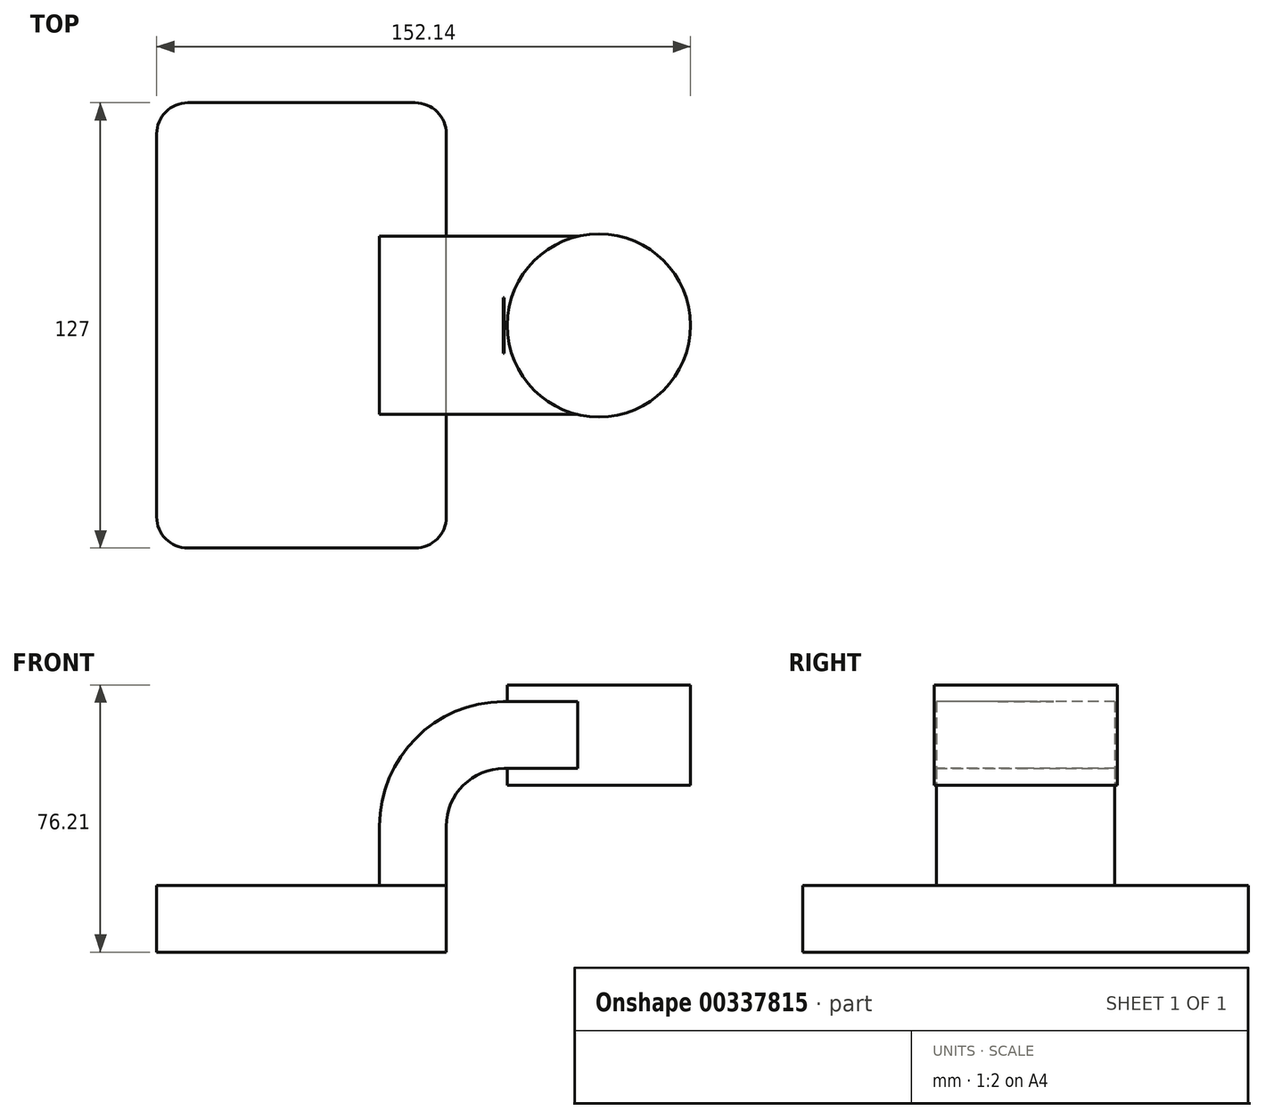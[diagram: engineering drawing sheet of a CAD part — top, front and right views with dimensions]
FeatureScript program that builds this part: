
annotation { "Feature Type Name" : "Feature", "Feature Type Description" : "" }
export const myFeature = defineFeature(function(context is Context, id is Id, definition is map)
    precondition{}
    {
        {
            var Q0;
            Q0=qCreatedBy(makeId("Front.planeOp"),FACE);
            var sketch = newSketch(context, id + "F0", { "sketchPlane" : qUnion([Q0])});
            skLineSegment(sketch, "E0.bottom", {"start": v(41.28, -9.52) * mm, "end": v(-41.28, -9.53) * mm});
            skLineSegment(sketch, "E0.top", {"start": v(41.28, 9.53) * mm, "end": v(-41.28, 9.53) * mm});
            skLineSegment(sketch, "E0.left", {"start": v(41.28, -9.52) * mm, "end": v(41.28, 9.53) * mm});
            skLineSegment(sketch, "E0.right", {"start": v(-41.28, -9.53) * mm, "end": v(-41.28, 9.53) * mm});
            skPoint(sketch, "E0.middle", {"position": v(0, 0) * mm});
            skLineSegment(sketch, "E1.bottom", {"start": v(110.87, 66.68) * mm, "end": v(60.07, 66.68) * mm});
            skLineSegment(sketch, "E1.top", {"start": v(110.87, 38.1) * mm, "end": v(60.07, 38.1) * mm});
            skLineSegment(sketch, "E1.left", {"start": v(60.07, 38.1) * mm, "end": v(60.07, 66.68) * mm});
            skLineSegment(sketch, "E1.right", {"start": v(110.87, 38.1) * mm, "end": v(110.87, 66.68) * mm});
            skPoint(sketch, "E1.middle", {"position": v(85.47, 52.39) * mm});
            skLineSegment(sketch, "E2", {"start": v(41.28, 9.53) * mm, "end": v(41.28, 26.37) * mm});
            skArc(sketch, "E3", {"start": v(41.27, 26.37) * mm, "mid": v(46.11, 38.04) * mm, "end": v(57.78, 42.88) * mm});
            skLineSegment(sketch, "E4", {"start": v(57.78, 42.88) * mm, "end": v(84.75, 42.88) * mm});
            skLineSegment(sketch, "E5.0", {"start": v(57.78, 61.93) * mm, "end": v(84.75, 61.93) * mm});
            skArc(sketch, "E5.1", {"start": v(22.22, 26.37) * mm, "mid": v(32.64, 51.5) * mm, "end": v(57.79, 61.93) * mm});
            skLineSegment(sketch, "E5.2", {"start": v(22.22, 9.53) * mm, "end": v(22.22, 26.37) * mm});
            skLineSegment(sketch, "E6", {"start": v(84.75, 38.1) * mm, "end": v(84.75, 66.68) * mm});
            skPoint(sketch, "E6.startSnap0", {"position": v(85.47, 38.1) * mm});
            skFitSpline(sketch, "E7", {"points": [v(-41.28, 9.52) * mm, v(57.78, 61.93) * mm], "startDerivative": vector(1.78, 88.63) * mm, "endDerivative": vector(147.71, 0.36) * mm});
            skSolve(sketch);
        }
        {
            var Q0;
            Q0=makeQuery(id+"F0.imprint","IMPRINT",FACE,{"disambiguationData":[TD([[makeQuery(id+"F0.imprint","IMPRINT",EDGE,{"derivedFrom":sQuery(id+"F0.wireOp",EDGE,"E0.bottom")}),-1.0]])]});
            extrude(context, id + "F1", {"entities" : qUnion([Q0]), "endBound" : BoundingType.SYMMETRIC, "depth" : 127 * mm});
        }
        {
            var Q0;
            {var subQ1=sQuery(id+"F0.wireOp",EDGE,"E2");Q0=makeQuery(id+"F0.imprint","IMPRINT",FACE,{"disambiguationData":[TD([[makeQuery(id+"F0.imprint","IMPRINT",EDGE,{"derivedFrom":subQ1}),1.0]])]});}
            var Q1;
            {var subQ0=sQuery(id+"F0.wireOp",EDGE,"E4");var subQ1=sQuery(id+"F0.wireOp",EDGE,"E1.left");var subQ2=makeQuery(id+"F0.imprint","INTERSECT",VERTEX,{"derivedFrom":[subQ1,subQ0]});Q1=makeQuery(id+"F0.imprint","IMPRINT",FACE,{"disambiguationData":[TD([[makeQuery(id+"F0.imprint","IMPRINT",EDGE,{"disambiguationData":[TD([[subQ2,-1.0]])],"derivedFrom":subQ1}),-1.0]])]});}
            extrude(context, id + "F2", {"entities" : qUnion([Q0, Q1]), "endBound" : BoundingType.SYMMETRIC, "depth" : 50.8 * mm});
        }
        {
            var Q0;
            Q0=makeQuery(id+"F0.imprint","IMPRINT",FACE,{"disambiguationData":[TD([[makeQuery(id+"F0.imprint","IMPRINT",EDGE,{"derivedFrom":sQuery(id+"F0.wireOp",EDGE,"E5.1")}),1.0]])]});
            extrude(context, id + "F3", {"entities" : qUnion([Q0]), "endBound" : BoundingType.SYMMETRIC, "depth" : 15.88 * mm});
        }
        {
            var Q0;
            {var subQ4=sQuery(id+"F0.wireOp",EDGE,"E1.right");Q0=makeQuery(id+"F0.imprint","IMPRINT",FACE,{"disambiguationData":[TD([[makeQuery(id+"F0.imprint","IMPRINT",EDGE,{"derivedFrom":subQ4}),1.0]])]});}
            var Q1;
            Q1=sQuery(id+"F0.wireOp",EDGE,"E6");
            revolve(context, id + "F4", {"operationType" : NewBodyOperationType.ADD, "entities" : qUnion([Q0]), "axis" : qUnion([Q1]), "revolveType" : RevolveType.FULL});
        }
        {
            var Q0;
            Q0=makeQuery(id+"F1.opExtrude","CAP_EDGE",EDGE,{"disambiguationData":[OSD([sQuery(id+"F0.wireOp",EDGE,"E0.left")])],"isStart":false});
            var Q1;
            Q1=makeQuery(id+"F1.opExtrude","CAP_EDGE",EDGE,{"disambiguationData":[OSD([sQuery(id+"F0.wireOp",EDGE,"E0.right")])],"isStart":false});
            var Q2;
            Q2=makeQuery(id+"F1.opExtrude","CAP_EDGE",EDGE,{"disambiguationData":[OSD([sQuery(id+"F0.wireOp",EDGE,"E0.left")])],"isStart":true});
            var Q3;
            Q3=makeQuery(id+"F1.opExtrude","CAP_EDGE",EDGE,{"disambiguationData":[OSD([sQuery(id+"F0.wireOp",EDGE,"E0.right")])],"isStart":true});
            fillet(context, id + "F5", {"entities" : qUnion([Q0, Q1, Q2, Q3]), "radius" : 8.9 * mm, "tangentPropagation" : true, "allowEdgeOverflow" : false});
        }
    });
